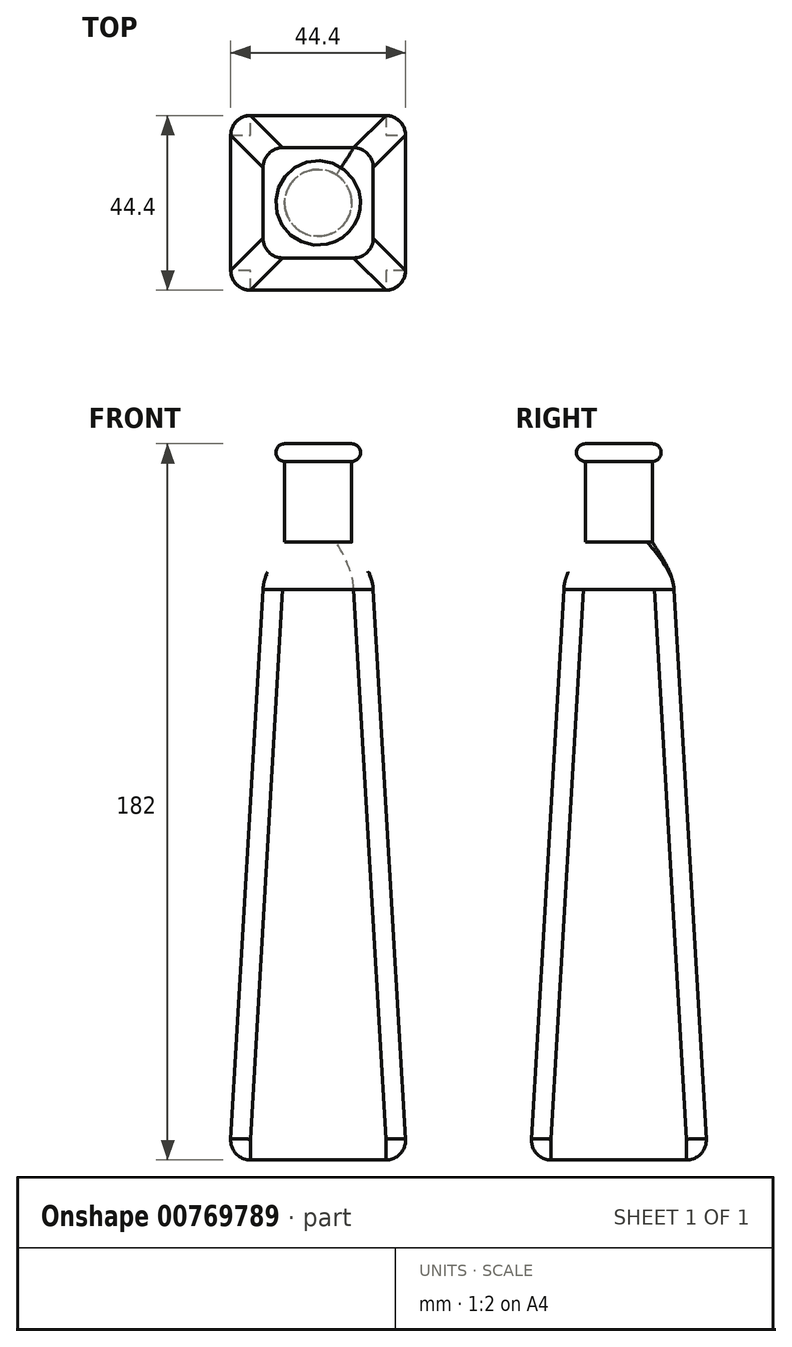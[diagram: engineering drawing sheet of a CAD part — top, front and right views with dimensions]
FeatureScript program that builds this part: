
annotation { "Feature Type Name" : "Feature", "Feature Type Description" : "" }
export const myFeature = defineFeature(function(context is Context, id is Id, definition is map)
    precondition{}
    {
        {
            var Q0;
            Q0=qCreatedBy(makeId("Top.planeOp"),FACE);
            var sketch = newSketch(context, id + "F0", { "sketchPlane" : qUnion([Q0])});
            skLineSegment(sketch, "E0.bottom", {"start": v(17.5, 22.5) * mm, "end": v(-17.5, 22.5) * mm});
            skLineSegment(sketch, "E0.top", {"start": v(17.5, -22.5) * mm, "end": v(-17.5, -22.5) * mm});
            skLineSegment(sketch, "E0.left", {"start": v(22.5, 17.5) * mm, "end": v(22.5, -17.5) * mm});
            skLineSegment(sketch, "E0.right", {"start": v(-22.5, 17.5) * mm, "end": v(-22.5, -17.5) * mm});
            skPoint(sketch, "E0.middle", {"position": v(0, 0) * mm});
            skPoint(sketch, "E1.visualSharp", {"position": v(-22.5, 22.5) * mm});
            skArc(sketch, "E1.filletArc", {"start": v(-17.5, 22.5) * mm, "mid": v(-21.04, 21.04) * mm, "end": v(-22.5, 17.5) * mm});
            skPoint(sketch, "E2.visualSharp", {"position": v(22.5, 22.5) * mm});
            skArc(sketch, "E2.filletArc", {"start": v(22.5, 17.5) * mm, "mid": v(21.04, 21.04) * mm, "end": v(17.5, 22.5) * mm});
            skPoint(sketch, "E3.visualSharp", {"position": v(22.5, -22.5) * mm});
            skArc(sketch, "E3.filletArc", {"start": v(17.5, -22.5) * mm, "mid": v(21.04, -21.04) * mm, "end": v(22.5, -17.5) * mm});
            skPoint(sketch, "E4.visualSharp", {"position": v(-22.5, -22.5) * mm});
            skArc(sketch, "E4.filletArc", {"start": v(-22.5, -17.5) * mm, "mid": v(-21.04, -21.04) * mm, "end": v(-17.5, -22.5) * mm});
            skSolve(sketch);
        }
        {
            var Q0;
            Q0=qCreatedBy(makeId("Top.planeOp"),FACE);
            cPlane(context, id + "F1", {"entities" : qUnion([Q0]), "cplaneType" : CPlaneType.OFFSET, "offset" : 145 * mm, "width" : 150 * mm, "height" : 150 * mm});
        }
        {
            var Q0;
            Q0=qCreatedBy(id+"F1.planeOp",FACE);
            var sketch = newSketch(context, id + "F2", { "sketchPlane" : qUnion([Q0])});
            skLineSegment(sketch, "E5.bottom", {"start": v(9, 14) * mm, "end": v(-9, 14) * mm});
            skLineSegment(sketch, "E5.top", {"start": v(9, -14) * mm, "end": v(-9, -14) * mm});
            skLineSegment(sketch, "E5.left", {"start": v(14, 9) * mm, "end": v(14, -9) * mm});
            skLineSegment(sketch, "E5.right", {"start": v(-14, 9) * mm, "end": v(-14, -9) * mm});
            skPoint(sketch, "E5.middle", {"position": v(0, 0) * mm});
            skPoint(sketch, "E6.visualSharp", {"position": v(-14, 14) * mm});
            skArc(sketch, "E6.filletArc", {"start": v(-9, 14) * mm, "mid": v(-12.54, 12.54) * mm, "end": v(-14, 9) * mm});
            skPoint(sketch, "E7.visualSharp", {"position": v(14, 14) * mm});
            skArc(sketch, "E7.filletArc", {"start": v(14, 9) * mm, "mid": v(12.54, 12.54) * mm, "end": v(9, 14) * mm});
            skPoint(sketch, "E8.visualSharp", {"position": v(14, -14) * mm});
            skArc(sketch, "E8.filletArc", {"start": v(9, -14) * mm, "mid": v(12.54, -12.54) * mm, "end": v(14, -9) * mm});
            skPoint(sketch, "E9.visualSharp", {"position": v(-14, -14) * mm});
            skArc(sketch, "E9.filletArc", {"start": v(-14, -9) * mm, "mid": v(-12.54, -12.54) * mm, "end": v(-9, -14) * mm});
            skSolve(sketch);
        }
        {
            var Q0;
            Q0=qCreatedBy(id+"F1.planeOp",FACE);
            cPlane(context, id + "F3", {"entities" : qUnion([Q0]), "cplaneType" : CPlaneType.OFFSET, "offset" : 12 * mm, "width" : 150 * mm, "height" : 150 * mm});
        }
        {
            var Q0;
            Q0=qCreatedBy(id+"F3.planeOp",FACE);
            var sketch = newSketch(context, id + "F4", { "sketchPlane" : qUnion([Q0])});
            skCircle(sketch, "E10", {"center": v(0, 0) * mm, "radius": 8.5 * mm});
            skSolve(sketch);
        }
        {
            var Q0;
            Q0=makeQuery(id+"F0.imprint","IMPRINT",FACE,{"disambiguationData":[TD([[makeQuery(id+"F0.imprint","IMPRINT",EDGE,{"derivedFrom":sQuery(id+"F0.wireOp",EDGE,"E0.bottom")}),1.0]])]});
            var Q1;
            Q1=makeQuery(id+"F2.imprint","IMPRINT",FACE,{"disambiguationData":[TD([[makeQuery(id+"F2.imprint","IMPRINT",EDGE,{"derivedFrom":sQuery(id+"F2.wireOp",EDGE,"E5.bottom")}),1.0]])]});
            loft(context, id + "F5", {"sheetProfilesArray" : [{ "sheetProfileEntities" : qUnion([Q0]) }, { "sheetProfileEntities" : qUnion([Q1]) }]});
        }
        {
            var Q1;
            Q1=makeQuery(id+"F5.opLoft","CAP_FACE",FACE,{"disambiguationData":[OSD([makeQuery(id+"F2.imprint","IMPRINT",FACE,{"disambiguationData":[TD([[makeQuery(id+"F2.imprint","IMPRINT",EDGE,{"derivedFrom":sQuery(id+"F2.wireOp",EDGE,"E5.bottom")}),1.0]])]})])],"isStart":true});
            var Q2;
            Q2=makeQuery(id+"F4.imprint","IMPRINT",FACE,{"disambiguationData":[TD([[makeQuery(id+"F4.imprint","IMPRINT",EDGE,{"derivedFrom":sQuery(id+"F4.wireOp",EDGE,"E10")}),1.0]])]});
            loft(context, id + "F6", {"operationType" : NewBodyOperationType.ADD, "startCondition" : LoftEndDerivativeType.MATCH_TANGENT, "startMagnitude" : 1, "sheetProfilesArray" : [{ "sheetProfileEntities" : qUnion([Q1]) }, { "sheetProfileEntities" : qUnion([Q2]) }]});
        }
        {
            var Q0;
            Q0=makeQuery(id+"F6.opLoft","CAP_FACE",FACE,{"disambiguationData":[OSD([makeQuery(id+"F4.imprint","IMPRINT",FACE,{"disambiguationData":[TD([[makeQuery(id+"F4.imprint","IMPRINT",EDGE,{"derivedFrom":sQuery(id+"F4.wireOp",EDGE,"E10")}),1.0]])]})])],"isStart":true});
            extrude(context, id + "F7", {"entities" : qUnion([Q0]), "operationType" : NewBodyOperationType.ADD, "depth" : 25 * mm, "offsetDistance" : 25 * mm});
        }
        {
            var Q0;
            Q0=makeQuery(id+"F5.opLoft","MID_CAP_EDGE",EDGE,{"disambiguationData":[OSD([sQuery(id+"F0.wireOp",EDGE,"E0.top"),sQuery(id+"F0.wireOp",EDGE,"E3.filletArc"),sQuery(id+"F0.wireOp",EDGE,"E4.filletArc")])],"capPos":0.0});
            var Q1;
            Q1=makeQuery(id+"F5.opLoft","MID_CAP_EDGE",EDGE,{"disambiguationData":[OSD([sQuery(id+"F0.wireOp",EDGE,"E0.top"),sQuery(id+"F0.wireOp",EDGE,"E0.left"),sQuery(id+"F0.wireOp",EDGE,"E3.filletArc")])],"capPos":0.0});
            var Q2;
            Q2=makeQuery(id+"F5.opLoft","MID_CAP_EDGE",EDGE,{"disambiguationData":[OSD([sQuery(id+"F0.wireOp",EDGE,"E0.left"),sQuery(id+"F0.wireOp",EDGE,"E2.filletArc"),sQuery(id+"F0.wireOp",EDGE,"E3.filletArc")])],"capPos":0.0});
            fillet(context, id + "F8", {"entities" : qUnion([Q0, Q1, Q2]), "radius" : 5 * mm, "tangentPropagation" : true, "allowEdgeOverflow" : false});
        }
        {
            var Q0;
            Q0=qCreatedBy(makeId("Right.planeOp"),FACE);
            var sketch = newSketch(context, id + "F9", { "sketchPlane" : qUnion([Q0])});
            skLineSegment(sketch, "E11", {"start": v(-8.5, 157) * mm, "end": v(-8.5, 182) * mm});
            skFitSpline(sketch, "E12.0", {"points": [v(-7.15, 182) * mm, v(-7.6, 182) * mm, v(-8.05, 182) * mm, v(-8.5, 182) * mm]});
            skArc(sketch, "E13", {"start": v(-8.5, 182) * mm, "mid": v(-10.76, 179.74) * mm, "end": v(-8.5, 177.48) * mm});
            skFitSpline(sketch, "E14.0.0", {"points": [v(7.15, 182) * mm, v(7.6, 182) * mm, v(8.05, 182) * mm, v(8.5, 182) * mm]});
            skFitSpline(sketch, "E14.0.1", {"points": [v(8.3, 182) * mm, v(7.07, 182) * mm, v(5.83, 182) * mm, v(4.6, 182) * mm]});
            skFitSpline(sketch, "E14.0.2", {"points": [v(4.6, 182) * mm, v(2.46, 182) * mm, v(0.33, 182) * mm, v(-1.8, 182) * mm]});
            skFitSpline(sketch, "E14.0.3", {"points": [v(-1.8, 182) * mm, v(-3.59, 182) * mm, v(-5.37, 182) * mm, v(-7.15, 182) * mm]});
            skFitSpline(sketch, "E14.0.4", {"points": [v(-7.15, 182) * mm, v(-7.6, 182) * mm, v(-8.05, 182) * mm, v(-8.5, 182) * mm]});
            skFitSpline(sketch, "E14.0.5", {"points": [v(-8.3, 182) * mm, v(-7.07, 182) * mm, v(-5.83, 182) * mm, v(-4.6, 182) * mm]});
            skFitSpline(sketch, "E14.0.6", {"points": [v(-4.6, 182) * mm, v(-2.46, 182) * mm, v(-0.33, 182) * mm, v(1.8, 182) * mm]});
            skFitSpline(sketch, "E14.0.7", {"points": [v(1.8, 182) * mm, v(3.59, 182) * mm, v(5.37, 182) * mm, v(7.15, 182) * mm]});
            skLineSegment(sketch, "E15", {"start": v(0, 0) * mm, "end": v(0, 182) * mm, "construction": true});
            skSolve(sketch);
        }
        {
            var Q0;
            {var subQ0=sQuery(id+"F9.wireOp",EDGE,"E13");Q0=makeQuery(id+"F9.imprint","IMPRINT",FACE,{"disambiguationData":[TD([[makeQuery(id+"F9.imprint","IMPRINT",EDGE,{"derivedFrom":subQ0}),1.0]])]});}
            var Q1;
            Q1=sQuery(id+"F9.wireOp",EDGE,"E15");
            revolve(context, id + "F10", {"operationType" : NewBodyOperationType.ADD, "surfaceOperationType" : NewSurfaceOperationType.NEW, "entities" : qUnion([Q0]), "axis" : qUnion([Q1]), "revolveType" : RevolveType.FULL});
        }
    });
